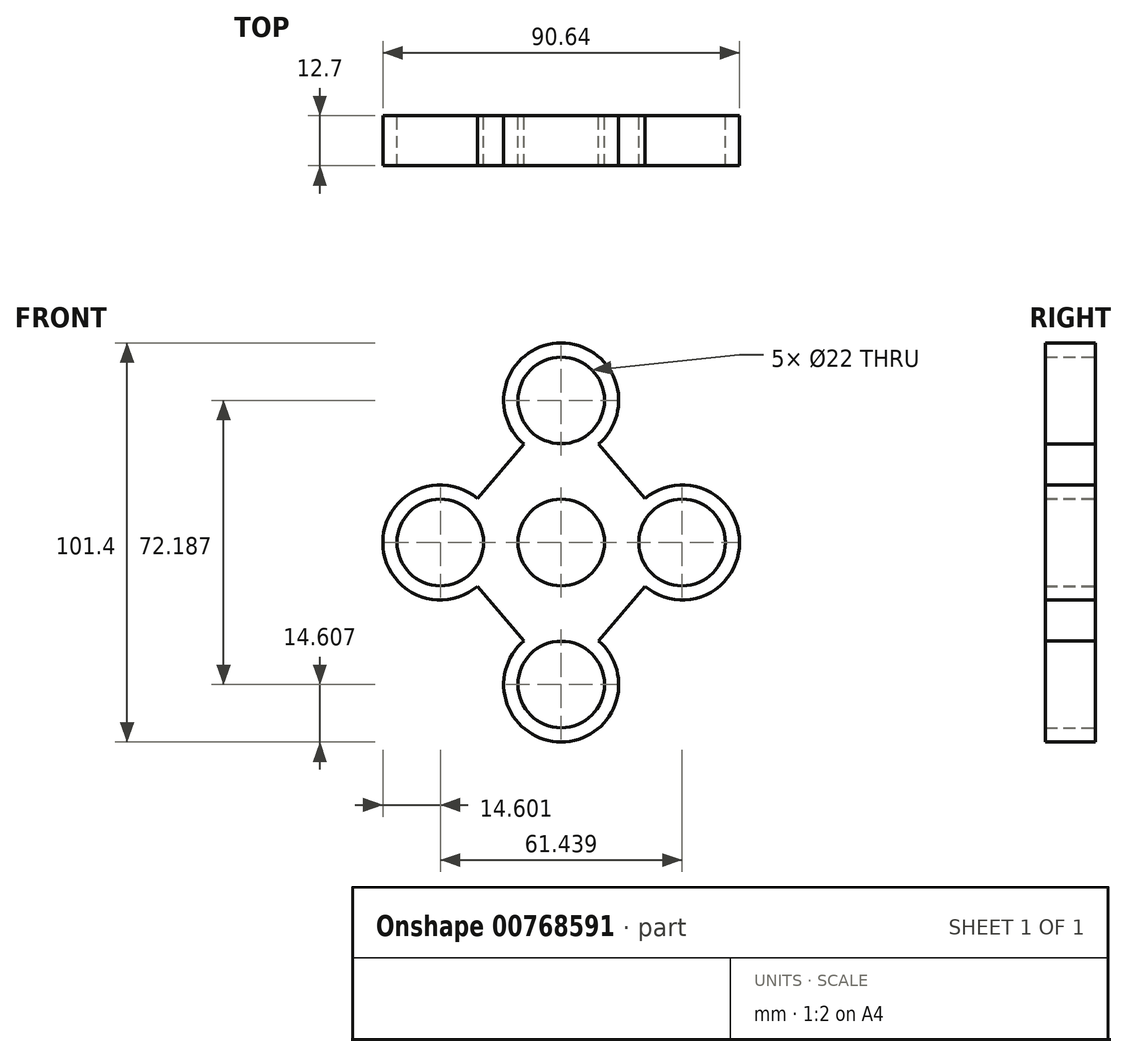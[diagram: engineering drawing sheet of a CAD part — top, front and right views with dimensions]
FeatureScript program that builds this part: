
annotation { "Feature Type Name" : "Feature", "Feature Type Description" : "" }
export const myFeature = defineFeature(function(context is Context, id is Id, definition is map)
    precondition{}
    {
        {
            var Q0;
            Q0=qCreatedBy(makeId("Front.planeOp"),FACE);
            var sketch = newSketch(context, id + "F0", { "sketchPlane" : qUnion([Q0])});
            skCircle(sketch, "E0", {"center": v(0, 0) * mm, "radius": 11 * mm});
            skLineSegment(sketch, "E1", {"start": v(7.13, 27.72) * mm, "end": v(23.6, 8.38) * mm});
            skLineSegment(sketch, "E2", {"start": v(23.6, -8.38) * mm, "end": v(7.13, -27.72) * mm});
            skLineSegment(sketch, "E3", {"start": v(-7.13, -27.72) * mm, "end": v(-23.6, -8.38) * mm});
            skLineSegment(sketch, "E4", {"start": v(-23.6, 8.38) * mm, "end": v(-7.13, 27.72) * mm});
            skCircle(sketch, "E5", {"center": v(0, 36.1) * mm, "radius": 11 * mm});
            skCircle(sketch, "E6", {"center": v(30.72, 0) * mm, "radius": 11 * mm});
            skCircle(sketch, "E7", {"center": v(0, -36.1) * mm, "radius": 11 * mm});
            skCircle(sketch, "E8", {"center": v(-30.72, 0) * mm, "radius": 11 * mm});
            skArc(sketch, "E9", {"start": v(-21.25, 11.12) * mm, "mid": v(-45.32, 0) * mm, "end": v(-21.25, -11.12) * mm});
            skArc(sketch, "E10", {"start": v(-9.47, -24.97) * mm, "mid": v(0, -50.7) * mm, "end": v(9.47, -24.97) * mm});
            skArc(sketch, "E11", {"start": v(21.25, -11.12) * mm, "mid": v(45.32, 0) * mm, "end": v(21.25, 11.12) * mm});
            skArc(sketch, "E12", {"start": v(9.47, 24.97) * mm, "mid": v(0, 50.7) * mm, "end": v(-9.47, 24.97) * mm});
            skSolve(sketch);
        }
        {
            var Q0;
            Q0 = qSketchRegion(id + "F0", true);
            extrude(context, id + "F1", {"entities" : qUnion([Q0]), "depth" : 12.7 * mm, "offsetDistance" : 25.4 * mm});
        }
    });
